# Revit family: ConcealedCistern-ForGypsumplateWalls-RapidInstallation-8cm-WCPanConcealedCisterns-Vitra_748-5800-02
name_source: partatom
category: Plumbing Fixtures
revit_build: Autodesk Revit 2017 (Build: 20160225_1515(x64)
units: mm (PartAtom-declared; Revit-internal decimal feet)

## family parameters
Cut with Voids When Loaded = No
Host = Face
OmniClass Number = 23.45.05.21.11
OmniClass Title = Water Closets
Part Type = Normal
Room Calculation Point = No
Round Connector Dimension = Use Diameter
Shared = Yes

## types (3) — shared parameters
BIMobject category = Toilet Cisterns
Brand = Vitra
CW Connection = Yes
Default Elevation = 1000 mm  [stored 3.28084 ft]
Design country = Turkey
First Material = White
Flush Plate  (.min 25  .max 70) = 70 mm
HW Connection = No
IFC Classification = Sanitary Terminal
Main Material = Plastic
Manufacturer = Vitra
Manufacturer name = Vitra
MountingType = Assembly to floor
NBS Referans Code = 35-93-90
NBS Referans Description = Wc Cisterns
Nominal Depth (mm) = 130 mm  [stored 0.426509 ft]
Nominal Height (mm) = 1125 mm
Nominal Width (mm) = 535 mm  [stored 1.75525 ft]
OmniClass Code = 23-31 19 19
OmniClass Description = Water Closets
Product certification = https://vitraglobal.com
Product data url = https://www.vitraglobal.com
Secondary Material = Yellow
Technical description = https://www.vitraglobal.com
URL = https://www.vitra.com.tr
Uniclass 2.0 Code = PR-35-93-90
Uniclass 2.0 Description = Wc Cisterns
Uniclass 2015 Code = Pr_40_20_93_89
Uniclass 2015 Name = WC cisterns
Vent Connection = No
WC Pan Connection (.max 340) = 340 mm  [stored 1.11549 ft]
Warranty Period (Year) = 10 Years
Waste Connection = Yes
Weight Net (kg) = 17,600
Youtube = https://www.youtube.com
zero-valued in all types: Cost

## per-type parameters (varying)
| type | Article No. (default) | Description | Model | Product Manual | Product SKU | Product group |
| ConcealedCistern-8cm-2,5/4lt-WCPanConcealedCisterns-Vitra_748-5800-02 | 748-5800-02 | Rapid Installation - 2,5/4 Liter Concealed Cistern Set (Pre-Wall Gypsumplate Wall) - 8 cm - Assembly to wall | 748-5800-02 | Rapid Installation - 2,5/4 Liter Concealed Cistern Set (Pre-Wall Gypsumplate Wall) - 8 cm - Assembly to wall | 748-5800-02 | Rapid Installation - 2,5/4 Liter Concealed Cistern Set (Pre-Wall Gypsumplate Wall) - 8 cm - Assembly to wall |
| ConcealedCistern-8cm-3/6lt-WCPanConcealedCisterns-Vitra_748-5800-01 | 748-5800-01 | Rapid Installation - 3/6 Liter Concealed Cistern Set (Pre-Wall Gypsumplate Wall) - 8 cm - Assembly to wall | 748-5800-01 | Rapid Installation - 3/6 Liter Concealed Cistern Set (Pre-Wall Gypsumplate Wall) - 8 cm - Assembly to wall | 748-5800-01 | Rapid Installation - 3/6 Liter Concealed Cistern Set (Pre-Wall Gypsumplate Wall) - 8 cm - Assembly to wall |
| ConcealedCistern-8cm-3/6lt-WCPanConcealedCisterns-Vitra_748-5800-01IND | 748-5800-01IND | Rapid Installation - 3/6 Liter Concealed Cistern Set (Pre-Wall Gypsumplate Wall) - 8 cm - Assembly to wall | 748-5800-01IND | Rapid Installation - 3/6 Liter Concealed Cistern Set (Pre-Wall Gypsumplate Wall) - 8 cm - Assembly to wall | 748-5800-01IND | Rapid Installation - 3/6 Liter Concealed Cistern Set (Pre-Wall Gypsumplate Wall) - 8 cm - Assembly to wall |

note: [stored X ft] marks values corroborated as IEEE doubles in the binary element streams (Revit-internal decimal feet)

## geometry (parser evidence)
native form markers: Sweep x2
no freeform markers — native parametric forms only
